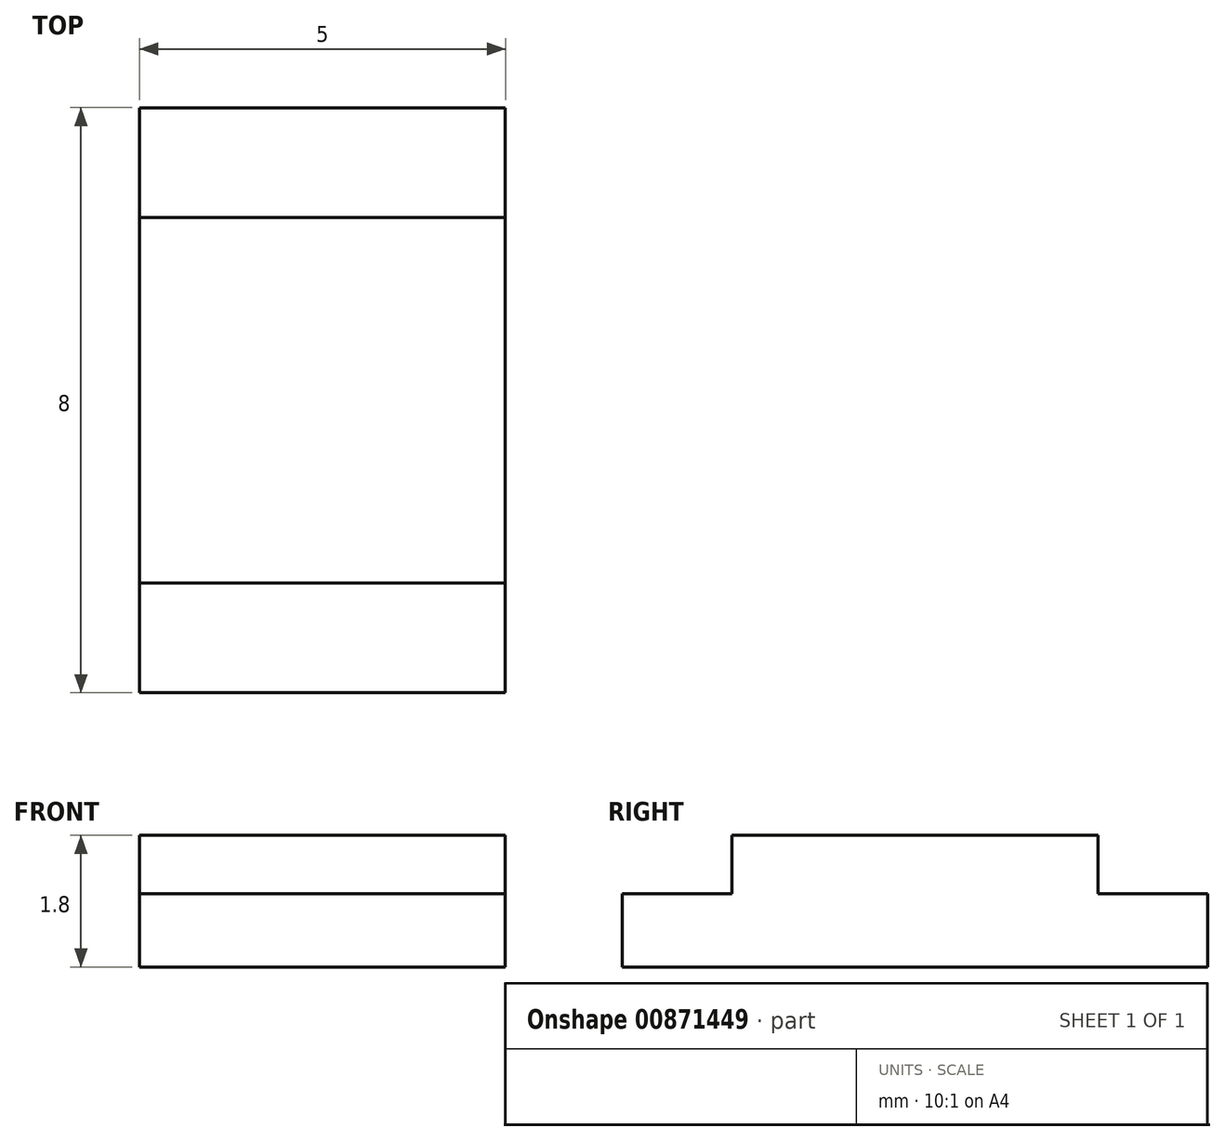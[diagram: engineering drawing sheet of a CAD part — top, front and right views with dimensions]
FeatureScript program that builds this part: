
annotation { "Feature Type Name" : "Feature", "Feature Type Description" : "" }
export const myFeature = defineFeature(function(context is Context, id is Id, definition is map)
    precondition{}
    {
        {
            var Q0;
            Q0=qCreatedBy(makeId("Top.planeOp"),FACE);
            var sketch = newSketch(context, id + "F0", { "sketchPlane" : qUnion([Q0])});
            skLineSegment(sketch, "E0.bottom", {"start": v(-4.87, -2.67) * mm, "end": v(0.13, -2.67) * mm});
            skLineSegment(sketch, "E0.top", {"start": v(-4.87, 5.33) * mm, "end": v(0.13, 5.33) * mm});
            skLineSegment(sketch, "E0.left", {"start": v(-4.87, -2.67) * mm, "end": v(-4.87, 5.33) * mm});
            skLineSegment(sketch, "E0.right", {"start": v(0.13, -2.67) * mm, "end": v(0.13, 5.33) * mm});
            skSolve(sketch);
        }
        {
            var Q0;
            Q0=makeQuery(id+"F0.imprint","IMPRINT",FACE,{"disambiguationData":[TD([[makeQuery(id+"F0.imprint","IMPRINT",EDGE,{"derivedFrom":sQuery(id+"F0.wireOp",EDGE,"E0.bottom")}),1.0]])]});
            extrude(context, id + "F1", {"entities" : qUnion([Q0]), "depth" : 1 * mm, "offsetDistance" : 25 * mm});
        }
        {
            var Q0;
            Q0=makeQuery(id+"F1.opExtrude","CAP_FACE",FACE,{"disambiguationData":[OSD([sQuery(id+"F0.wireOp",EDGE,"E0.bottom"),sQuery(id+"F0.wireOp",EDGE,"E0.top"),sQuery(id+"F0.wireOp",EDGE,"E0.left"),sQuery(id+"F0.wireOp",EDGE,"E0.right")])],"isStart":false});
            var sketch = newSketch(context, id + "F2", { "sketchPlane" : qUnion([Q0])});
            skLineSegment(sketch, "E1.bottom", {"start": v(-4.87, -1.17) * mm, "end": v(0.13, -1.17) * mm});
            skLineSegment(sketch, "E1.top", {"start": v(-4.87, 3.83) * mm, "end": v(0.13, 3.83) * mm});
            skLineSegment(sketch, "E1.left", {"start": v(-4.87, -1.17) * mm, "end": v(-4.87, 3.83) * mm});
            skLineSegment(sketch, "E1.right", {"start": v(0.13, -1.17) * mm, "end": v(0.13, 3.83) * mm});
            skPoint(sketch, "E2", {"position": v(-4.87, 1.33) * mm});
            skSolve(sketch);
        }
        {
            var Q0;
            Q0=makeQuery(id+"F2.imprint","IMPRINT",FACE,{"disambiguationData":[TD([[makeQuery(id+"F2.imprint","IMPRINT",EDGE,{"derivedFrom":sQuery(id+"F2.wireOp",EDGE,"E1.bottom")}),1.0]])]});
            extrude(context, id + "F3", {"entities" : qUnion([Q0]), "operationType" : NewBodyOperationType.ADD, "depth" : .8 * mm, "offsetDistance" : 25 * mm});
        }
    });
